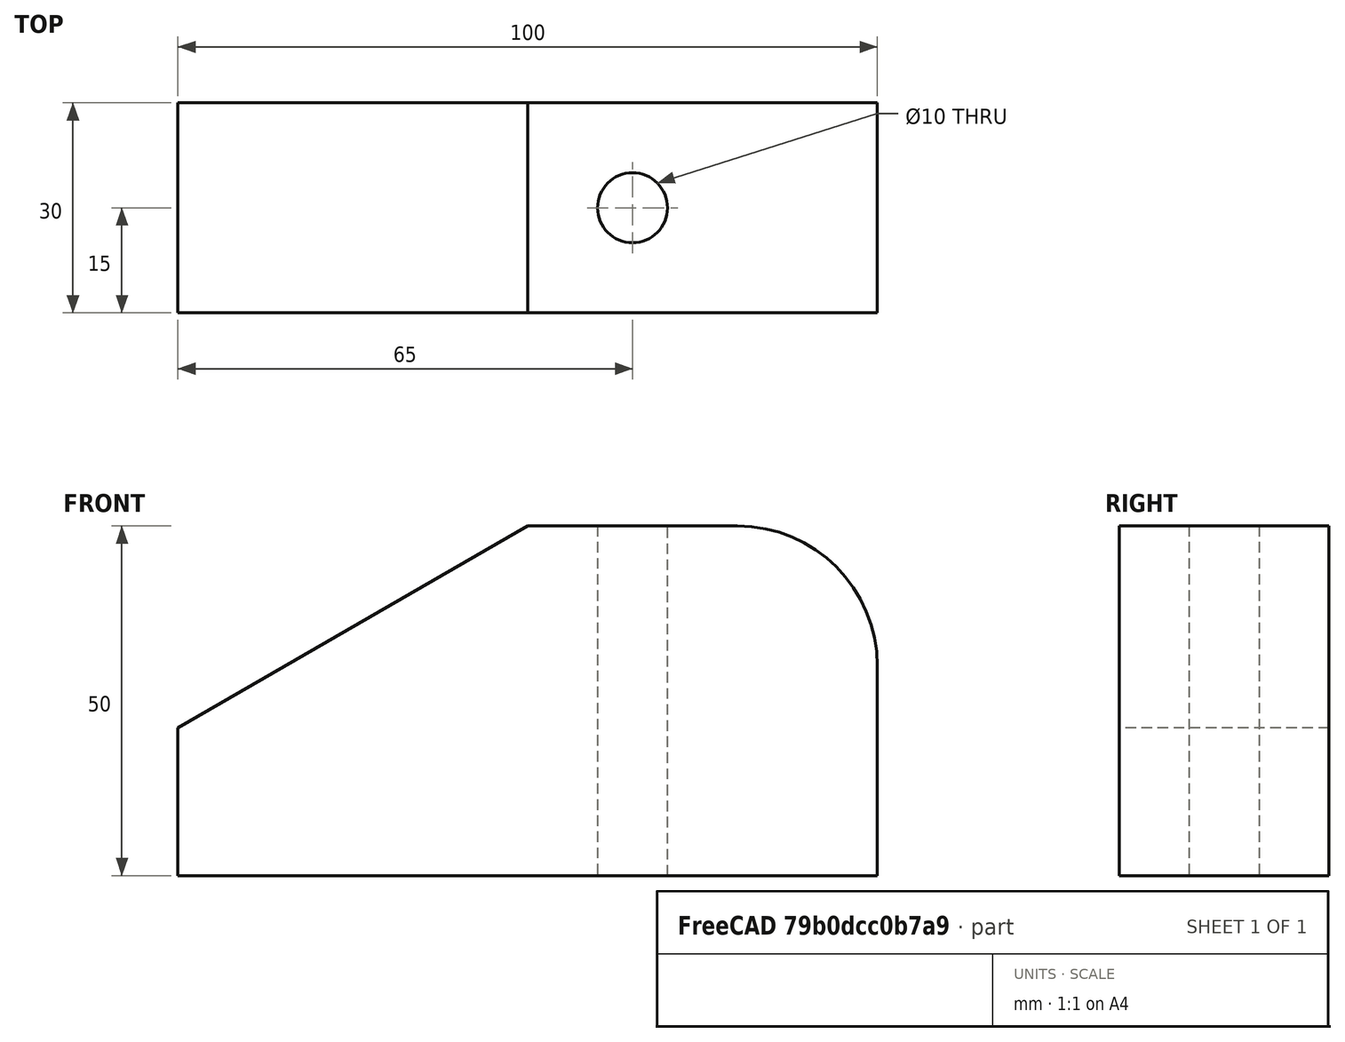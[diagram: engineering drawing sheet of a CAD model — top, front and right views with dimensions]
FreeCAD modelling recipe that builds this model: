
FCSTD DOCUMENT  (FreeCAD 0.20R29410 (Git))
Label: Creating a simple part with Part WB_Positioning_Chamfer
License: All rights reserved
LicenseURL: http://en.wikipedia.org/wiki/All_rights_reserved
objects: Part::Box×2, Part::Cut×2, Part::Fillet×1, Part::Cylinder×1
note: 6 computed .brp shape members not serialized (recipe doc carries the construction recipe); baked Part::Feature solids carry a one-line shape summary decoded from their .brp

FEATURE [Part::Box] Box  label="Cube"
  AttacherType = Attacher::AttachEngine3D
  Height = 50
  Length = 100
  Width = 30
FEATURE [Part::Fillet] Fillet
  Base = -> Box
  Edges = 1 edges r=20: [Edge6]
FEATURE [Part::Box] Box001  label="Cube001"
  AttacherType = Attacher::AttachEngine3D
  Height = 60
  Length = 30
  Placement = pos=(50,0,50) rot=(0,1,0;-2.0944rad)
  Width = 30
FEATURE [Part::Cut] Cut
  Base = -> Fillet
  Tool = -> Box001
FEATURE [Part::Cylinder] Cylinder
  Angle = 360
  AttacherType = Attacher::AttachEngine3D
  FirstAngle = 0
  Height = 50
  Placement = pos=(65,15,0) rot=(0,0,1;0rad)
  Radius = 5
  SecondAngle = 0
FEATURE [Part::Cut] Cut001
  Base = -> Cut
  Tool = -> Cylinder
